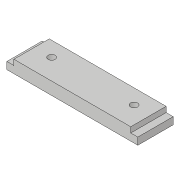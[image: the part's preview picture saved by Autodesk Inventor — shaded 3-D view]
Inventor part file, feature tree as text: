
AUTODESK INVENTOR PART (.ipt)
format: ipt  version: 2018.3 (Build 223284000, 284)  size: 138,752 bytes
history: native  units: in
note: dims shown in document units (in); Inventor stores cm internally (conversion verified against a paired STEP export)
features: extrude x3, sketch x3
ambient origin geometry x8: Origin, YZ Plane, XZ Plane, XY Plane, X Axis, Y Axis, Z Axis, Center Point
bodies: Solid1 (feature_tree)
feature tree (6):
  extrude  "Extrusion1"  Depth=0.625in
  extrude  "Extrusion6"  Depth=0.221in
  extrude  "Extrusion7"  Depth=0.096in
  sketch  "Sketch1"  dims[d0=2.315in d1=0.625in]
  sketch  "Sketch7"  dims[d2=0.221in d3=0.0in d22=0.126in]
  sketch  "Sketch8"  dims[d23=0.126in d24=1.4567in d32=1.0in d33=0.0in d34=0.125in d35=0.125in d36=0.096in d37=0.0in d43=0.2619in d44=0.2619in d48=0.429in d49=0.4293in]
